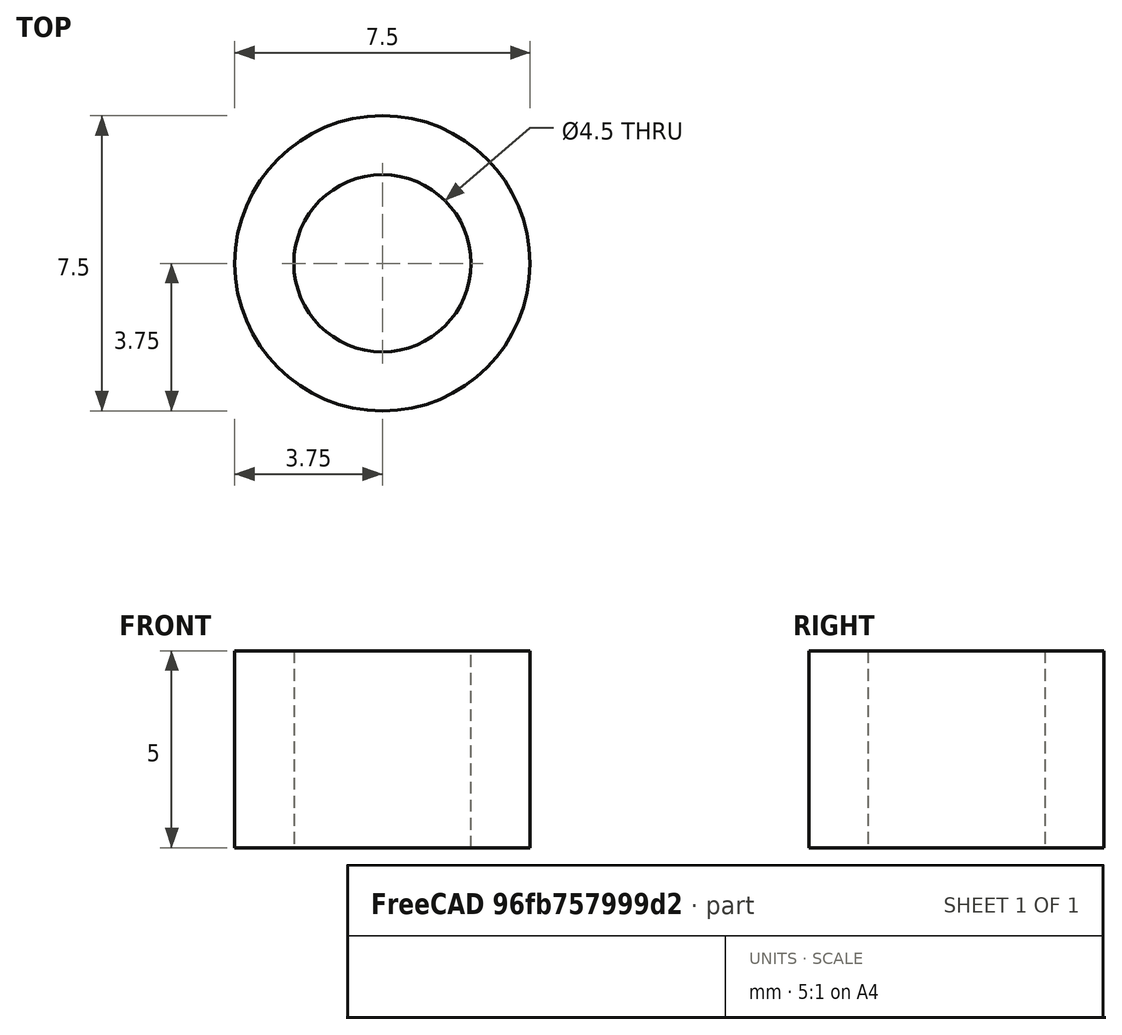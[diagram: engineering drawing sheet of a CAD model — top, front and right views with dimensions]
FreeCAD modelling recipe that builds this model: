
FCSTD DOCUMENT  (FreeCAD 0.22R37841 (Git))
Label: FanSpacers
License: All rights reserved
LicenseURL: http://en.wikipedia.org/wiki/All_rights_reserved
objects: Sketcher::SketchObject×1, PartDesign::Pad×1, PartDesign::Body×1
note: 4 computed .brp shape members not serialized (recipe doc carries the construction recipe); baked Part::Feature solids carry a one-line shape summary decoded from their .brp

FEATURE [Sketcher::SketchObject] Sketch
  AttachmentSupport = -> [XY_Plane]
  FullyConstrained = true
  MapMode = 5
  sketch-geometry (2):
    g0: Circle CenterX=0 CenterY=0 CenterZ=0 NormalX=0 NormalY=0 NormalZ=1 AngleXU=0 Radius=3.75
    g1: Circle CenterX=0 CenterY=0 CenterZ=0 NormalX=0 NormalY=0 NormalZ=1 AngleXU=0 Radius=2.25
  constraints (4):
    c: Coincident(g0,g-1)
    c: Diameter(g0) = 7.5
    c: Coincident(g1,g0)
    c: Diameter(g1) = 4.5
FEATURE [PartDesign::Pad] Pad
  Direction = (0,0,1)
  Length = 5
  Length2 = 10
  Profile = -> Sketch
  ReferenceAxis = -> Sketch [N_Axis]
  Suppressed = false
  Type = 0
FEATURE [PartDesign::Body] Body
  AllowCompound = false
  Group = -> [Sketch,Pad]
  Origin = -> Origin
  Tip = -> Pad
